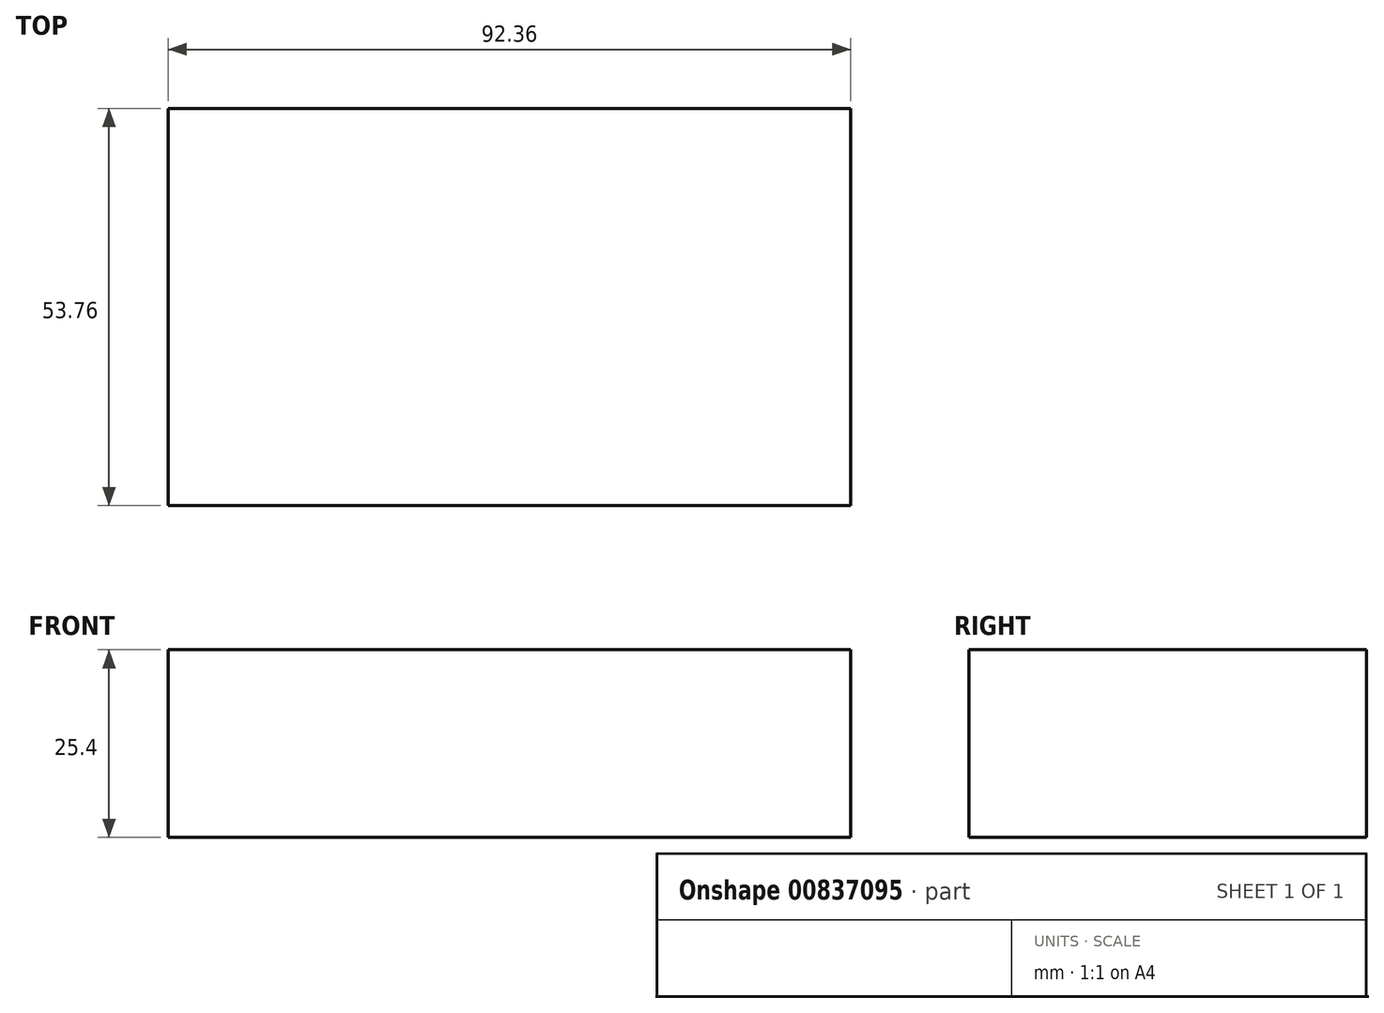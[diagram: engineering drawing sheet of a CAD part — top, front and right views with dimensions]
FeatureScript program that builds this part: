
annotation { "Feature Type Name" : "Feature", "Feature Type Description" : "" }
export const myFeature = defineFeature(function(context is Context, id is Id, definition is map)
    precondition{}
    {
        {
            var Q0;
            Q0=qCreatedBy(makeId("Top.planeOp"),FACE);
            var sketch = newSketch(context, id + "F0", { "sketchPlane" : qUnion([Q0])});
            skLineSegment(sketch, "E0.bottom", {"start": v(46.18, 26.88) * mm, "end": v(-46.18, 26.88) * mm});
            skLineSegment(sketch, "E0.top", {"start": v(46.18, -26.88) * mm, "end": v(-46.18, -26.88) * mm});
            skLineSegment(sketch, "E0.left", {"start": v(46.18, 26.88) * mm, "end": v(46.18, -26.88) * mm});
            skLineSegment(sketch, "E0.right", {"start": v(-46.18, 26.88) * mm, "end": v(-46.18, -26.88) * mm});
            skPoint(sketch, "E0.middle", {"position": v(0, 0) * mm});
            skSolve(sketch);
        }
        {
            var Q0;
            Q0=makeQuery(id+"F0.imprint","IMPRINT",FACE,{"disambiguationData":[TD([[makeQuery(id+"F0.imprint","IMPRINT",EDGE,{"derivedFrom":sQuery(id+"F0.wireOp",EDGE,"E0.bottom")}),1.0]])]});
            var Q1;
            Q1=sQuery(id+"F0.wireOp",EDGE,"E0.bottom");
            extrude(context, id + "F1", {"entities" : qUnion([Q0]), "surfaceEntities" : qUnion([Q1]), "depth" : 25.4 * mm, "offsetDistance" : 25.4 * mm});
        }
    });
